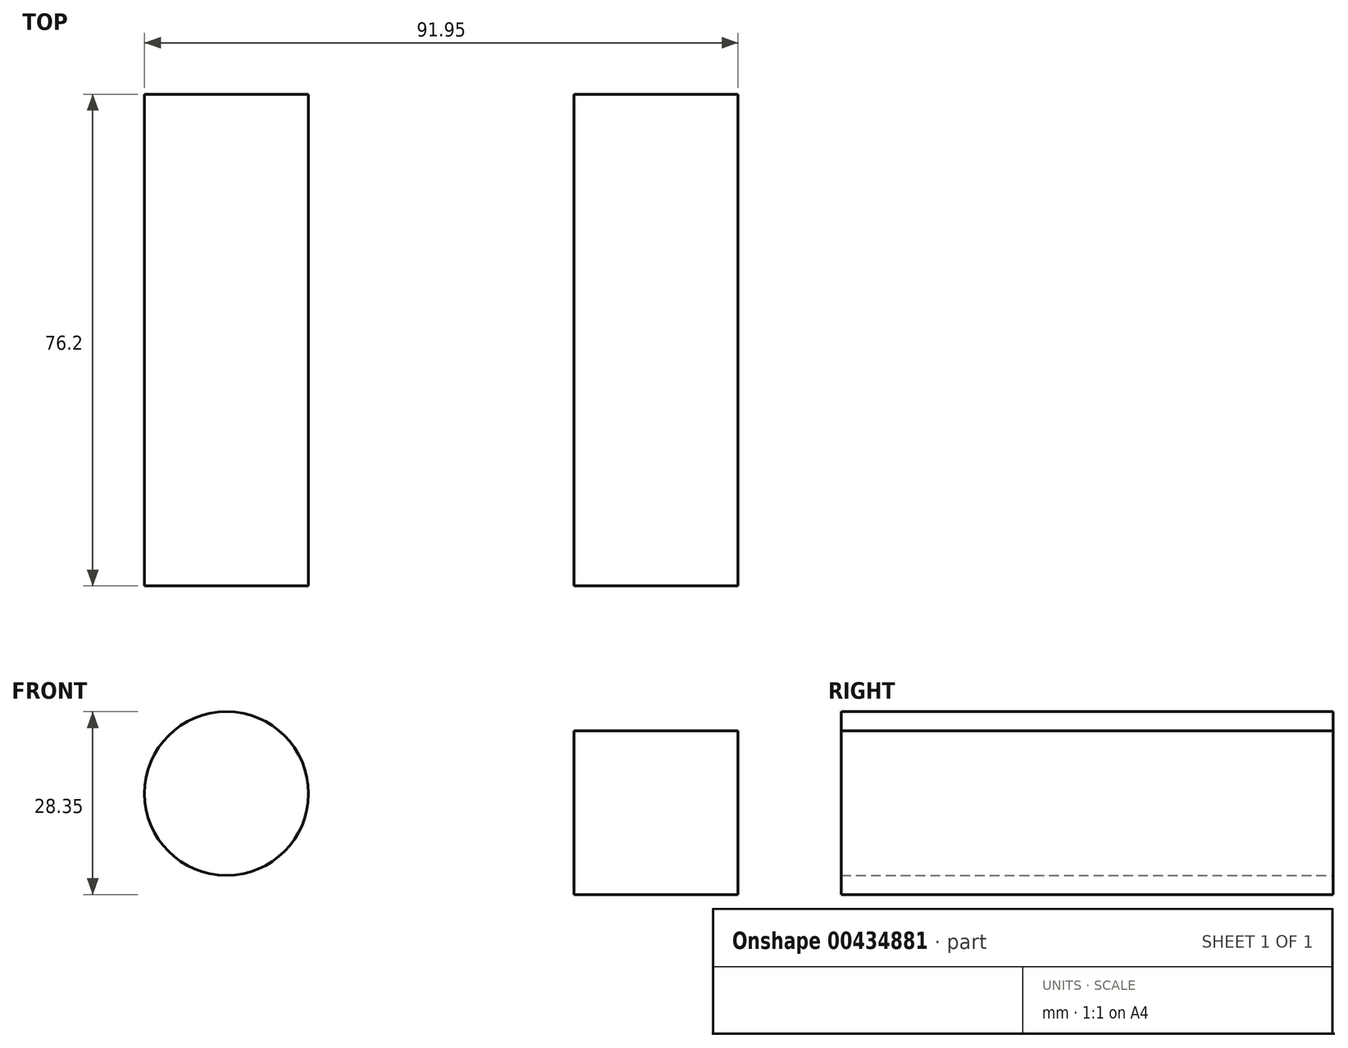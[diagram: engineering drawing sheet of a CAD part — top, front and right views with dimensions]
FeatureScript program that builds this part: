
annotation { "Feature Type Name" : "Feature", "Feature Type Description" : "" }
export const myFeature = defineFeature(function(context is Context, id is Id, definition is map)
    precondition{}
    {
        {
            var Q0;
            Q0=qCreatedBy(makeId("Front.planeOp"),FACE);
            var sketch = newSketch(context, id + "F0", { "sketchPlane" : qUnion([Q0])});
            skCircle(sketch, "E0", {"center": v(-35.9, 18.9) * mm, "radius": 12.7 * mm});
            skLineSegment(sketch, "E1.bottom", {"start": v(17.95, 28.65) * mm, "end": v(43.35, 28.65) * mm});
            skLineSegment(sketch, "E1.top", {"start": v(17.95, 3.25) * mm, "end": v(43.35, 3.25) * mm});
            skLineSegment(sketch, "E1.left", {"start": v(17.95, 28.65) * mm, "end": v(17.95, 3.25) * mm});
            skLineSegment(sketch, "E1.right", {"start": v(43.35, 28.65) * mm, "end": v(43.35, 3.25) * mm});
            skSolve(sketch);
        }
        {
            var Q0;
            Q0=makeQuery(id+"F0.imprint","IMPRINT",FACE,{"disambiguationData":[TD([[makeQuery(id+"F0.imprint","IMPRINT",EDGE,{"derivedFrom":sQuery(id+"F0.wireOp",EDGE,"E0")}),1.0]])]});
            var Q1;
            Q1=makeQuery(id+"F0.imprint","IMPRINT",FACE,{"disambiguationData":[TD([[makeQuery(id+"F0.imprint","IMPRINT",EDGE,{"derivedFrom":sQuery(id+"F0.wireOp",EDGE,"E1.bottom")}),-1.0]])]});
            extrude(context, id + "F1", {"entities" : qUnion([Q0, Q1]), "depth" : 76.2 * mm});
        }
    });
